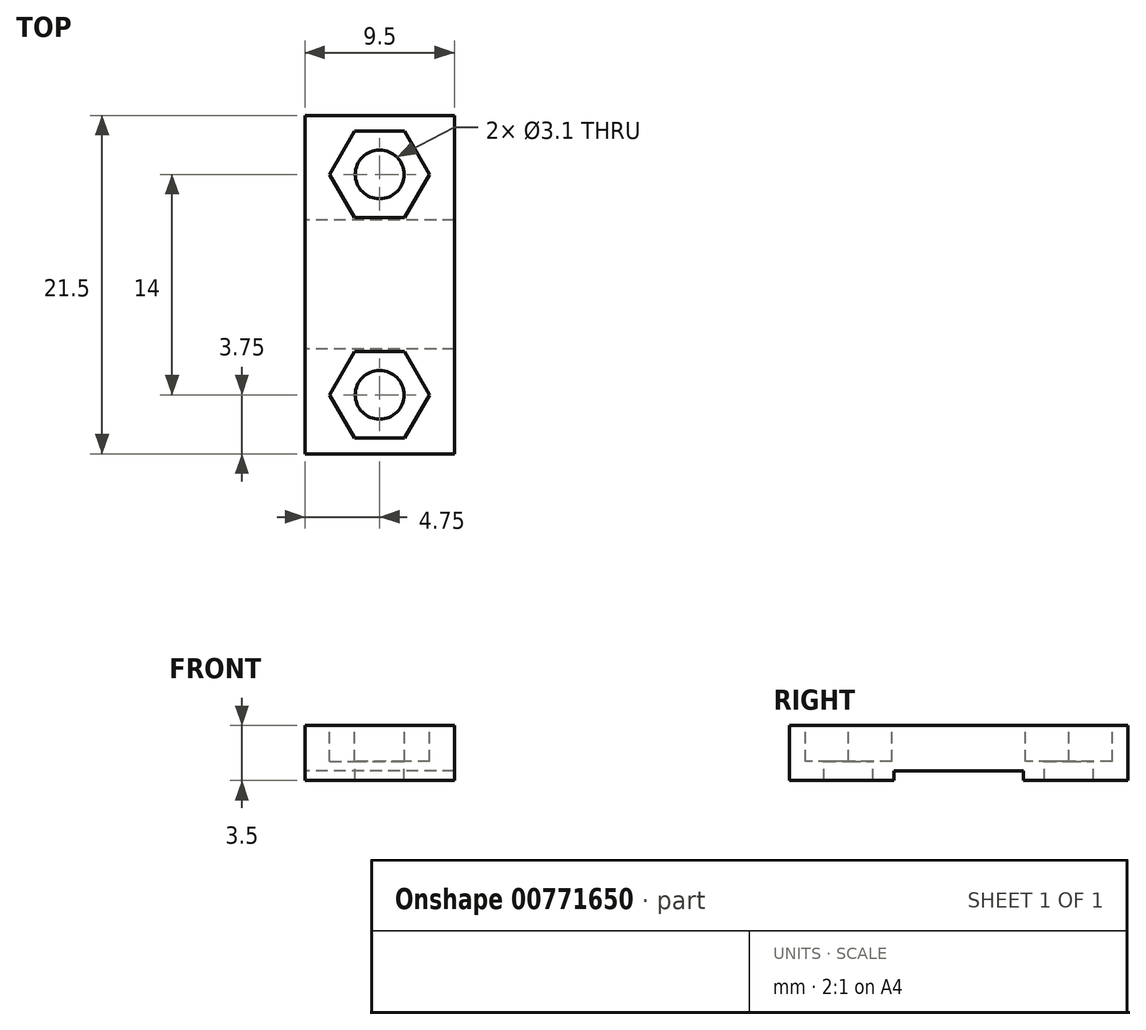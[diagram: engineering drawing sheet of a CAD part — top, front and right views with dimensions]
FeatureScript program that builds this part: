
annotation { "Feature Type Name" : "Feature", "Feature Type Description" : "" }
export const myFeature = defineFeature(function(context is Context, id is Id, definition is map)
    precondition{}
    {
        {
            var Q0;
            Q0=qCreatedBy(makeId("Top.planeOp"),FACE);
            var sketch = newSketch(context, id + "F0", { "sketchPlane" : qUnion([Q0])});
            skLineSegment(sketch, "E0.bottom", {"start": v(-4.75, 10.75) * mm, "end": v(4.75, 10.75) * mm});
            skLineSegment(sketch, "E0.top", {"start": v(-4.75, -10.75) * mm, "end": v(4.75, -10.75) * mm});
            skLineSegment(sketch, "E0.left", {"start": v(-4.75, 10.75) * mm, "end": v(-4.75, -10.75) * mm});
            skLineSegment(sketch, "E0.right", {"start": v(4.75, 10.75) * mm, "end": v(4.75, -10.75) * mm});
            skSolve(sketch);
        }
        {
            var Q0;
            Q0 = qSketchRegion(id + "F0", true);
            extrude(context, id + "F1", {"entities" : qUnion([Q0]), "depth" : 3.5 * mm, "offsetDistance" : 25 * mm});
        }
        {
            var Q0;
            Q0=makeQuery(id+"F1.opExtrude","CAP_FACE",FACE,{"disambiguationData":[OSD([sQuery(id+"F0.wireOp",EDGE,"E0.bottom"),sQuery(id+"F0.wireOp",EDGE,"E0.top"),sQuery(id+"F0.wireOp",EDGE,"E0.left"),sQuery(id+"F0.wireOp",EDGE,"E0.right")])],"isStart":false});
            var sketch = newSketch(context, id + "F2", { "sketchPlane" : qUnion([Q0])});
            skCircle(sketch, "E1", {"center": v(0, 7) * mm, "radius": 1.55 * mm});
            skCircle(sketch, "E2", {"center": v(0, -7) * mm, "radius": 1.55 * mm});
            skSolve(sketch);
        }
        {
            var Q0;
            Q0 = qSketchRegion(id + "F2", true);
            extrude(context, id + "F3", {"entities" : qUnion([Q0]), "operationType" : NewBodyOperationType.REMOVE, "endBound" : BoundingType.UP_TO_NEXT, "oppositeDirection" : true, "depth" : 25 * mm, "offsetDistance" : 25 * mm});
        }
        {
            var Q0;
            Q0=makeQuery(id+"F1.opExtrude","CAP_FACE",FACE,{"disambiguationData":[OSD([sQuery(id+"F0.wireOp",EDGE,"E0.bottom"),sQuery(id+"F0.wireOp",EDGE,"E0.top"),sQuery(id+"F0.wireOp",EDGE,"E0.left"),sQuery(id+"F0.wireOp",EDGE,"E0.right")])],"isStart":true});
            var sketch = newSketch(context, id + "F4", { "sketchPlane" : qUnion([Q0])});
            skLineSegment(sketch, "E3.bottom", {"start": v(4.75, -4.1) * mm, "end": v(-4.75, -4.1) * mm});
            skLineSegment(sketch, "E3.top", {"start": v(4.75, 4.1) * mm, "end": v(-4.75, 4.1) * mm});
            skLineSegment(sketch, "E3.left", {"start": v(4.75, -4.1) * mm, "end": v(4.75, 4.1) * mm});
            skLineSegment(sketch, "E3.right", {"start": v(-4.75, -4.1) * mm, "end": v(-4.75, 4.1) * mm});
            skSolve(sketch);
        }
        {
            var Q0;
            Q0 = qSketchRegion(id + "F4", true);
            extrude(context, id + "F5", {"entities" : qUnion([Q0]), "operationType" : NewBodyOperationType.REMOVE, "oppositeDirection" : true, "depth" : 0.6 * mm, "offsetDistance" : 25 * mm});
        }
        {
            var Q0;
            Q0=makeQuery(id+"F1.opExtrude","CAP_FACE",FACE,{"disambiguationData":[OSD([sQuery(id+"F0.wireOp",EDGE,"E0.bottom"),sQuery(id+"F0.wireOp",EDGE,"E0.top"),sQuery(id+"F0.wireOp",EDGE,"E0.left"),sQuery(id+"F0.wireOp",EDGE,"E0.right")])],"isStart":false});
            var sketch = newSketch(context, id + "F6", { "sketchPlane" : qUnion([Q0])});
            skCircle(sketch, "E4.cCircle", {"center": v(0, 7) * mm, "radius": 2.75 * mm, "construction": true});
            skLineSegment(sketch, "E4.0", {"start": v(3.18, 7) * mm, "end": v(1.59, 4.25) * mm});
            skLineSegment(sketch, "E4.1", {"start": v(1.59, 4.25) * mm, "end": v(-1.59, 4.25) * mm});
            skLineSegment(sketch, "E4.2", {"start": v(-1.59, 4.25) * mm, "end": v(-3.18, 7) * mm});
            skLineSegment(sketch, "E4.3", {"start": v(-3.18, 7) * mm, "end": v(-1.59, 9.75) * mm});
            skLineSegment(sketch, "E4.4", {"start": v(-1.59, 9.75) * mm, "end": v(1.59, 9.75) * mm});
            skLineSegment(sketch, "E4.5", {"start": v(1.59, 9.75) * mm, "end": v(3.18, 7) * mm});
            skPoint(sketch, "E4.0.midPoint", {"position": v(2.38, 5.62) * mm});
            skCircle(sketch, "E5.cCircle", {"center": v(0, -7) * mm, "radius": 2.75 * mm, "construction": true});
            skLineSegment(sketch, "E5.0", {"start": v(3.18, -7) * mm, "end": v(1.59, -9.75) * mm});
            skLineSegment(sketch, "E5.1", {"start": v(1.59, -9.75) * mm, "end": v(-1.59, -9.75) * mm});
            skLineSegment(sketch, "E5.2", {"start": v(-1.59, -9.75) * mm, "end": v(-3.18, -7) * mm});
            skLineSegment(sketch, "E5.3", {"start": v(-3.18, -7) * mm, "end": v(-1.59, -4.25) * mm});
            skLineSegment(sketch, "E5.4", {"start": v(-1.59, -4.25) * mm, "end": v(1.59, -4.25) * mm});
            skLineSegment(sketch, "E5.5", {"start": v(1.59, -4.25) * mm, "end": v(3.18, -7) * mm});
            skPoint(sketch, "E5.0.midPoint", {"position": v(2.38, -8.38) * mm});
            skSolve(sketch);
        }
        {
            var Q0;
            Q0 = qSketchRegion(id + "F6", true);
            extrude(context, id + "F7", {"entities" : qUnion([Q0]), "operationType" : NewBodyOperationType.REMOVE, "oppositeDirection" : true, "depth" : 2.3 * mm, "offsetDistance" : 25 * mm});
        }
    });
